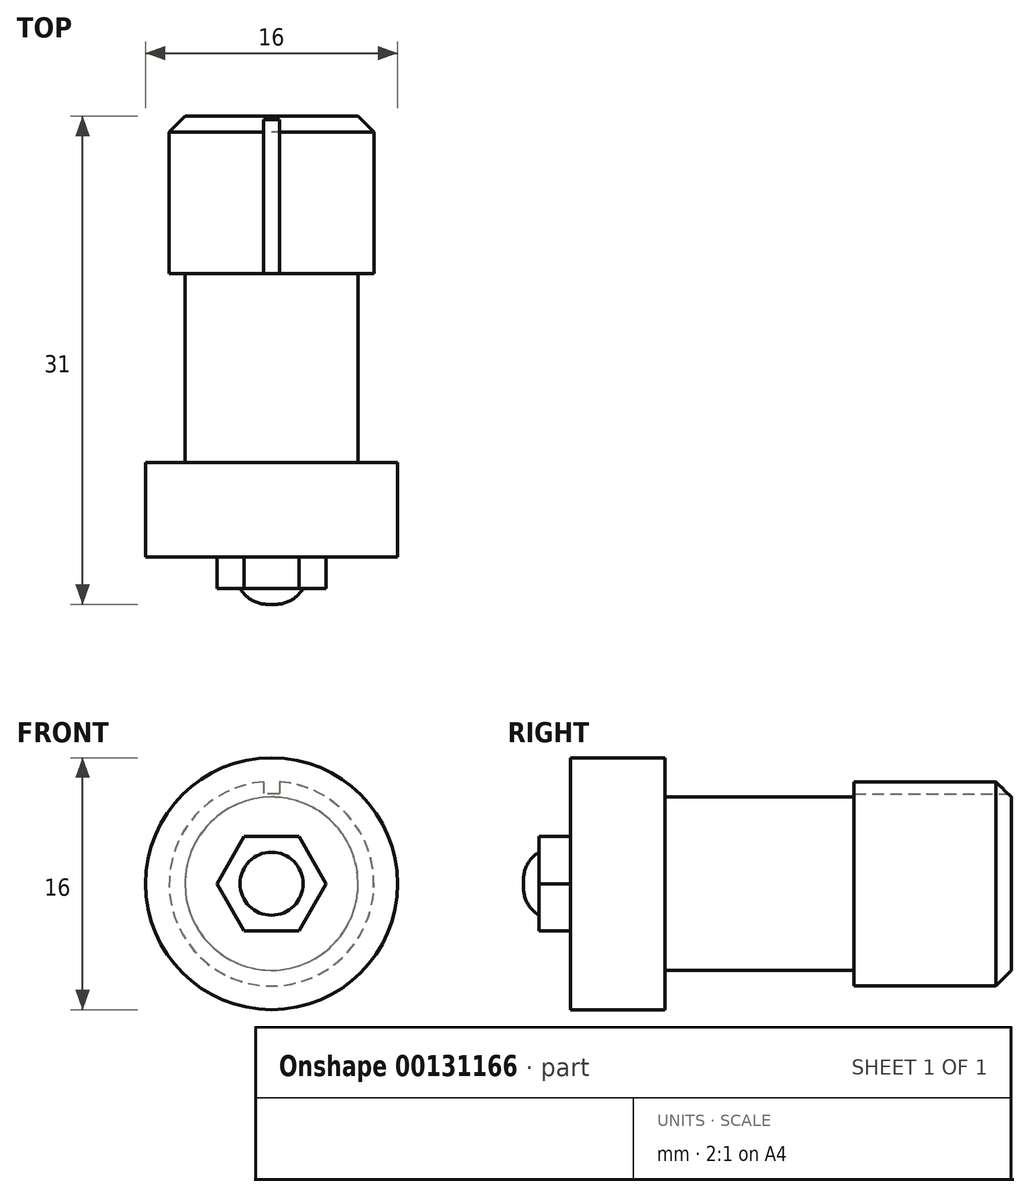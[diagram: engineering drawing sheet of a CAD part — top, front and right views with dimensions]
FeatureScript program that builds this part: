
annotation { "Feature Type Name" : "Feature", "Feature Type Description" : "" }
export const myFeature = defineFeature(function(context is Context, id is Id, definition is map)
    precondition{}
    {
        {
            var Q0;
            Q0=qCreatedBy(makeId("Front.planeOp"),FACE);
            var sketch = newSketch(context, id + "F0", { "sketchPlane" : qUnion([Q0])});
            skCircle(sketch, "E0", {"center": v(0, 0) * mm, "radius": 8 * mm});
            skSolve(sketch);
        }
        {
            var Q0;
            Q0=makeQuery(id+"F0.imprint","IMPRINT",FACE,{"disambiguationData":[TD([[makeQuery(id+"F0.imprint","IMPRINT",EDGE,{"derivedFrom":sQuery(id+"F0.wireOp",EDGE,"E0")}),1.0]])]});
            extrude(context, id + "F1", {"entities" : qUnion([Q0]), "oppositeDirection" : true, "depth" : 6 * mm});
        }
        {
            var Q0;
            Q0=makeQuery(id+"F1.opExtrude","CAP_FACE",FACE,{"disambiguationData":[OSD([sQuery(id+"F0.wireOp",EDGE,"E0")])],"isStart":true});
            var sketch = newSketch(context, id + "F2", { "sketchPlane" : qUnion([Q0])});
            skCircle(sketch, "E1.cCircle", {"center": v(0, 0) * mm, "radius": 3 * mm, "construction": true});
            skLineSegment(sketch, "E1.0", {"start": v(-1.73, 3) * mm, "end": v(1.73, 3) * mm});
            skLineSegment(sketch, "E1.1", {"start": v(1.73, 3) * mm, "end": v(3.46, 0) * mm});
            skLineSegment(sketch, "E1.2", {"start": v(3.46, 0) * mm, "end": v(1.73, -3) * mm});
            skLineSegment(sketch, "E1.3", {"start": v(1.73, -3) * mm, "end": v(-1.73, -3) * mm});
            skLineSegment(sketch, "E1.4", {"start": v(-1.73, -3) * mm, "end": v(-3.46, 0) * mm});
            skLineSegment(sketch, "E1.5", {"start": v(-3.46, 0) * mm, "end": v(-1.73, 3) * mm});
            skPoint(sketch, "E1.0.midPoint", {"position": v(0, 3) * mm});
            skSolve(sketch);
        }
        {
            var Q0;
            Q0=makeQuery(id+"F2.imprint","IMPRINT",FACE,{"disambiguationData":[TD([[makeQuery(id+"F2.imprint","IMPRINT",EDGE,{"derivedFrom":sQuery(id+"F2.wireOp",EDGE,"E1.0")}),-1.0]])]});
            extrude(context, id + "F3", {"entities" : qUnion([Q0]), "operationType" : NewBodyOperationType.ADD, "depth" : 2 * mm});
        }
        {
            var Q0;
            Q0=makeQuery(id+"F3.opExtrude","CAP_FACE",FACE,{"disambiguationData":[OSD([sQuery(id+"F2.wireOp",EDGE,"E1.0"),sQuery(id+"F2.wireOp",EDGE,"E1.1"),sQuery(id+"F2.wireOp",EDGE,"E1.2"),sQuery(id+"F2.wireOp",EDGE,"E1.3"),sQuery(id+"F2.wireOp",EDGE,"E1.4"),sQuery(id+"F2.wireOp",EDGE,"E1.5")])],"isStart":false});
            var sketch = newSketch(context, id + "F4", { "sketchPlane" : qUnion([Q0])});
            skCircle(sketch, "E2", {"center": v(0, 0) * mm, "radius": 2 * mm});
            skSolve(sketch);
        }
        {
            var Q0;
            Q0=makeQuery(id+"F4.imprint","IMPRINT",FACE,{"disambiguationData":[TD([[makeQuery(id+"F4.imprint","IMPRINT",EDGE,{"derivedFrom":sQuery(id+"F4.wireOp",EDGE,"E2")}),1.0]])]});
            extrude(context, id + "F5", {"entities" : qUnion([Q0]), "operationType" : NewBodyOperationType.ADD, "depth" : 1 * mm});
        }
        {
            var Q0;
            Q0=makeQuery(id+"F5.opExtrude","CAP_EDGE",EDGE,{"disambiguationData":[OSD([sQuery(id+"F4.wireOp",EDGE,"E2")])],"isStart":false});
            fillet(context, id + "F6", {"entities" : qUnion([Q0]), "radius" : 2 * mm, "tangentPropagation" : true, "allowEdgeOverflow" : false});
        }
        {
            var Q0;
            Q0=makeQuery(id+"F1.opExtrude","CAP_FACE",FACE,{"disambiguationData":[OSD([sQuery(id+"F0.wireOp",EDGE,"E0")])],"isStart":false});
            var sketch = newSketch(context, id + "F7", { "sketchPlane" : qUnion([Q0])});
            skCircle(sketch, "E3", {"center": v(0, 0) * mm, "radius": 5.5 * mm});
            skSolve(sketch);
        }
        {
            var Q0;
            Q0=makeQuery(id+"F7.imprint","IMPRINT",FACE,{"disambiguationData":[TD([[makeQuery(id+"F7.imprint","IMPRINT",EDGE,{"derivedFrom":sQuery(id+"F7.wireOp",EDGE,"E3")}),1.0]])]});
            extrude(context, id + "F8", {"entities" : qUnion([Q0]), "operationType" : NewBodyOperationType.ADD, "depth" : 22 * mm});
        }
        {
            var Q0;
            Q0=makeQuery(id+"F8.opExtrude","CAP_FACE",FACE,{"disambiguationData":[OSD([sQuery(id+"F7.wireOp",EDGE,"E3")])],"isStart":false});
            var sketch = newSketch(context, id + "F9", { "sketchPlane" : qUnion([Q0])});
            skCircle(sketch, "E4", {"center": v(0, 0) * mm, "radius": 6.5 * mm});
            skSolve(sketch);
        }
        {
            var Q0;
            Q0=makeQuery(id+"F9.imprint","IMPRINT",FACE,{"disambiguationData":[TD([[makeQuery(id+"F9.imprint","IMPRINT",EDGE,{"derivedFrom":sQuery(id+"F9.wireOp",EDGE,"E4")}),1.0]])]});
            extrude(context, id + "F10", {"entities" : qUnion([Q0]), "operationType" : NewBodyOperationType.ADD, "oppositeDirection" : true, "depth" : 10 * mm});
        }
        {
            var Q0;
            Q0=makeQuery(id+"F10.opExtrude","CAP_EDGE",EDGE,{"disambiguationData":[OSD([sQuery(id+"F9.wireOp",EDGE,"E4")])],"isStart":true});
            chamfer(context, id + "F11", {"entities" : qUnion([Q0]), "width" : 1 * mm, "tangentPropagation" : true});
        }
        {
            var Q0;
            {var subQ0=sQuery(id+"F7.wireOp",EDGE,"E3");Q0=makeQuery(id+"F10.boolean.opBoolean","MERGE",FACE,{"derivedFrom":[makeQuery(id+"F8.opExtrude","CAP_FACE",FACE,{"disambiguationData":[OSD([subQ0])],"isStart":false}),makeQuery(id+"F10.opExtrude","CAP_FACE",FACE,{"disambiguationData":[OSD([subQ0,sQuery(id+"F9.wireOp",EDGE,"E4")])],"isStart":true})]});}
            var sketch = newSketch(context, id + "F12", { "sketchPlane" : qUnion([Q0])});
            skLineSegment(sketch, "E5.bottom", {"start": v(-0.5, 7.7) * mm, "end": v(0.5, 7.7) * mm});
            skLineSegment(sketch, "E5.top", {"start": v(-0.5, 5.7) * mm, "end": v(0.5, 5.7) * mm});
            skLineSegment(sketch, "E5.left", {"start": v(-0.5, 7.7) * mm, "end": v(-0.5, 5.7) * mm});
            skLineSegment(sketch, "E5.right", {"start": v(0.5, 7.7) * mm, "end": v(0.5, 5.7) * mm});
            skLineSegment(sketch, "E6", {"start": v(0, 5.7) * mm, "end": v(0, 0) * mm, "construction": true});
            skSolve(sketch);
        }
        {
            var Q0;
            Q0=makeQuery(id+"F12.imprint","IMPRINT",FACE,{"disambiguationData":[TD([[makeQuery(id+"F12.imprint","IMPRINT",EDGE,{"derivedFrom":sQuery(id+"F12.wireOp",EDGE,"E5.bottom")}),-1.0]])]});
            extrude(context, id + "F13", {"entities" : qUnion([Q0]), "operationType" : NewBodyOperationType.REMOVE, "oppositeDirection" : true, "depth" : 20 * mm});
        }
    });
